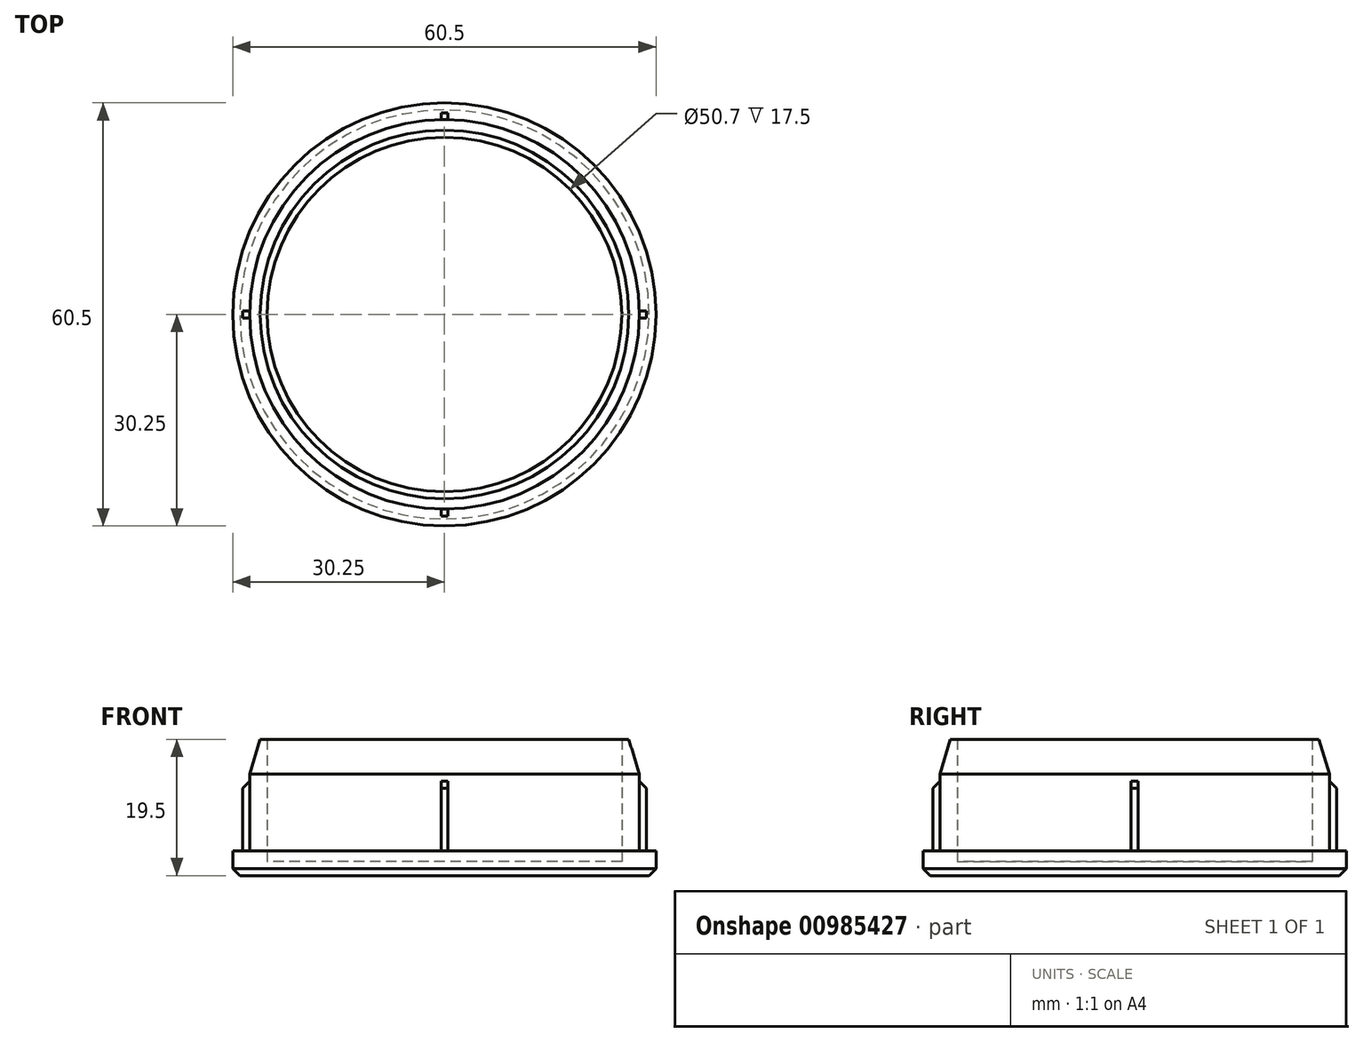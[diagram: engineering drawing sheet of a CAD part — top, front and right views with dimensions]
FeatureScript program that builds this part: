
annotation { "Feature Type Name" : "Feature", "Feature Type Description" : "" }
export const myFeature = defineFeature(function(context is Context, id is Id, definition is map)
    precondition{}
    {
        {
            var Q0;
            Q0=qCreatedBy(makeId("Top.planeOp"),FACE);
            var sketch = newSketch(context, id + "F0", { "sketchPlane" : qUnion([Q0])});
            skCircle(sketch, "E0", {"center": v(0, 0) * mm, "radius": 30.25 * mm});
            skSolve(sketch);
        }
        {
            var Q0;
            Q0=makeQuery(id+"F0.imprint","IMPRINT",FACE,{"disambiguationData":[TD([[makeQuery(id+"F0.imprint","IMPRINT",EDGE,{"derivedFrom":sQuery(id+"F0.wireOp",EDGE,"E0")}),1.0]])]});
            extrude(context, id + "F1", {"entities" : qUnion([Q0]), "depth" : 3.5 * mm, "offsetDistance" : 25 * mm});
        }
        {
            var Q0;
            Q0=makeQuery(id+"F1.opExtrude","CAP_FACE",FACE,{"disambiguationData":[OSD([sQuery(id+"F0.wireOp",EDGE,"E0")])],"isStart":false});
            var sketch = newSketch(context, id + "F2", { "sketchPlane" : qUnion([Q0])});
            skCircle(sketch, "E1", {"center": v(0, 0) * mm, "radius": 27.85 * mm});
            skCircle(sketch, "E2", {"center": v(0, 0) * mm, "radius": 25.35 * mm});
            skSolve(sketch);
        }
        {
            var Q0;
            Q0=makeQuery(id+"F2.imprint","IMPRINT",FACE,{"disambiguationData":[TD([[makeQuery(id+"F2.imprint","IMPRINT",EDGE,{"derivedFrom":sQuery(id+"F2.wireOp",EDGE,"E1")}),1.0]])]});
            var sketch = newSketch(context, id + "F3", { "sketchPlane" : qUnion([Q0])});
            skSolve(sketch);
        }
        {
            var Q0;
            Q0=makeQuery(id+"F3.imprint","IMPRINT",FACE,{"disambiguationData":[TD([[makeQuery(id+"F3.imprint","IMPRINT",EDGE,{"derivedFrom":makeQuery(id+"F2.imprint","IMPRINT",EDGE,{"derivedFrom":sQuery(id+"F2.wireOp",EDGE,"E1")})}),1.0]])]});
            extrude(context, id + "F4", {"entities" : qUnion([Q0]), "operationType" : NewBodyOperationType.ADD, "depth" : 10 * mm, "offsetDistance" : 25 * mm});
        }
        {
            var Q0;
            Q0=makeQuery(id+"F4.opExtrude","CAP_FACE",FACE,{"disambiguationData":[OSD([sQuery(id+"F2.wireOp",EDGE,"E1"),sQuery(id+"F2.wireOp",EDGE,"E2")])],"isStart":false});
            extrude(context, id + "F5", {"entities" : qUnion([Q0]), "operationType" : NewBodyOperationType.ADD, "depth" : 6 * mm, "offsetDistance" : 25 * mm});
        }
        {
            var Q0;
            Q0=makeQuery(id+"F5.opExtrude","CAP_EDGE",EDGE,{"disambiguationData":[OSD([sQuery(id+"F2.wireOp",EDGE,"E1")])],"isStart":false});
            chamfer(context, id + "F6", {"entities" : qUnion([Q0]), "chamferType" : ChamferType.TWO_OFFSETS, "width1" : 5 * mm, "oppositeDirection" : true, "width2" : 1.5 * mm, "tangentPropagation" : true});
        }
        {
            var Q0;
            {var subQ0=sQuery(id+"F0.wireOp",EDGE,"E0");Q0=makeQuery(id+"F4.boolean.opBoolean","SPLIT",FACE,{"disambiguationData":[TD([makeQuery(id+"F1.opExtrude","SWEPT_FACE",FACE,{"disambiguationData":[OSD([subQ0])]})])],"derivedFrom":makeQuery(id+"F1.opExtrude","CAP_FACE",FACE,{"disambiguationData":[OSD([subQ0])],"isStart":false})});}
            var sketch = newSketch(context, id + "F7", { "sketchPlane" : qUnion([Q0])});
            skLineSegment(sketch, "E3.bottom", {"start": v(0.5, -28.85) * mm, "end": v(-0.5, -28.85) * mm});
            skLineSegment(sketch, "E3.top", {"start": v(0.5, 28.85) * mm, "end": v(-0.5, 28.85) * mm});
            skLineSegment(sketch, "E3.left", {"start": v(0.5, -28.85) * mm, "end": v(0.5, 28.85) * mm});
            skLineSegment(sketch, "E3.right", {"start": v(-0.5, -28.85) * mm, "end": v(-0.5, 28.85) * mm});
            skPoint(sketch, "E3.middle", {"position": v(0, 0) * mm});
            skLineSegment(sketch, "E4.bottom", {"start": v(28.85, -0.5) * mm, "end": v(-28.85, -0.5) * mm});
            skLineSegment(sketch, "E4.top", {"start": v(28.85, 0.5) * mm, "end": v(-28.85, 0.5) * mm});
            skLineSegment(sketch, "E4.left", {"start": v(28.85, -0.5) * mm, "end": v(28.85, 0.5) * mm});
            skLineSegment(sketch, "E4.right", {"start": v(-28.85, -0.5) * mm, "end": v(-28.85, 0.5) * mm});
            skSolve(sketch);
        }
        {
            var Q0;
            {var subQ0=sQuery(id+"F7.wireOp",EDGE,"E4.left");Q0=makeQuery(id+"F7.imprint","IMPRINT",FACE,{"disambiguationData":[TD([[makeQuery(id+"F7.imprint","IMPRINT",EDGE,{"derivedFrom":subQ0}),1.0]])]});}
            var Q1;
            {var subQ0=sQuery(id+"F7.wireOp",EDGE,"E4.right");Q1=makeQuery(id+"F7.imprint","IMPRINT",FACE,{"disambiguationData":[TD([[makeQuery(id+"F7.imprint","IMPRINT",EDGE,{"derivedFrom":subQ0}),-1.0]])]});}
            var Q2;
            {var subQ0=sQuery(id+"F7.wireOp",EDGE,"E3.bottom");Q2=makeQuery(id+"F7.imprint","IMPRINT",FACE,{"disambiguationData":[TD([[makeQuery(id+"F7.imprint","IMPRINT",EDGE,{"derivedFrom":subQ0}),-1.0]])]});}
            var Q3;
            {var subQ0=sQuery(id+"F7.wireOp",EDGE,"E3.top");Q3=makeQuery(id+"F7.imprint","IMPRINT",FACE,{"disambiguationData":[TD([[makeQuery(id+"F7.imprint","IMPRINT",EDGE,{"derivedFrom":subQ0}),1.0]])]});}
            extrude(context, id + "F8", {"entities" : qUnion([Q0, Q1, Q2, Q3]), "operationType" : NewBodyOperationType.ADD, "depth" : 10 * mm, "offsetDistance" : 25 * mm});
        }
        {
            var Q0;
            Q0=makeQuery(id+"F8.opExtrude","CAP_EDGE",EDGE,{"disambiguationData":[OSD([sQuery(id+"F7.wireOp",EDGE,"E4.left")])],"isStart":false});
            var Q1;
            Q1=makeQuery(id+"F8.opExtrude","CAP_EDGE",EDGE,{"disambiguationData":[OSD([sQuery(id+"F7.wireOp",EDGE,"E3.top")])],"isStart":false});
            var Q2;
            Q2=makeQuery(id+"F8.opExtrude","CAP_EDGE",EDGE,{"disambiguationData":[OSD([sQuery(id+"F7.wireOp",EDGE,"E4.right")])],"isStart":false});
            var Q3;
            Q3=makeQuery(id+"F8.opExtrude","CAP_EDGE",EDGE,{"disambiguationData":[OSD([sQuery(id+"F7.wireOp",EDGE,"E3.bottom")])],"isStart":false});
            chamfer(context, id + "F9", {"entities" : qUnion([Q0, Q1, Q2, Q3]), "width" : 1 * mm, "tangentPropagation" : true});
        }
        {
            var Q0;
            Q0=makeQuery(id+"F4.boolean.opBoolean","SPLIT",FACE,{"disambiguationData":[TD([makeQuery(id+"F4.opExtrude","SWEPT_FACE",FACE,{"disambiguationData":[OSD([sQuery(id+"F2.wireOp",EDGE,"E2")])]})])],"derivedFrom":makeQuery(id+"F1.opExtrude","CAP_FACE",FACE,{"disambiguationData":[OSD([sQuery(id+"F0.wireOp",EDGE,"E0")])],"isStart":false})});
            extrude(context, id + "F10", {"entities" : qUnion([Q0]), "operationType" : NewBodyOperationType.REMOVE, "oppositeDirection" : true, "depth" : 1.5 * mm, "offsetDistance" : 25 * mm});
        }
        {
            var Q0;
            Q0=makeQuery(id+"F1.opExtrude","CAP_EDGE",EDGE,{"disambiguationData":[OSD([sQuery(id+"F0.wireOp",EDGE,"E0")])],"isStart":true});
            chamfer(context, id + "F11", {"entities" : qUnion([Q0]), "width" : 1 * mm, "tangentPropagation" : true});
        }
    });
